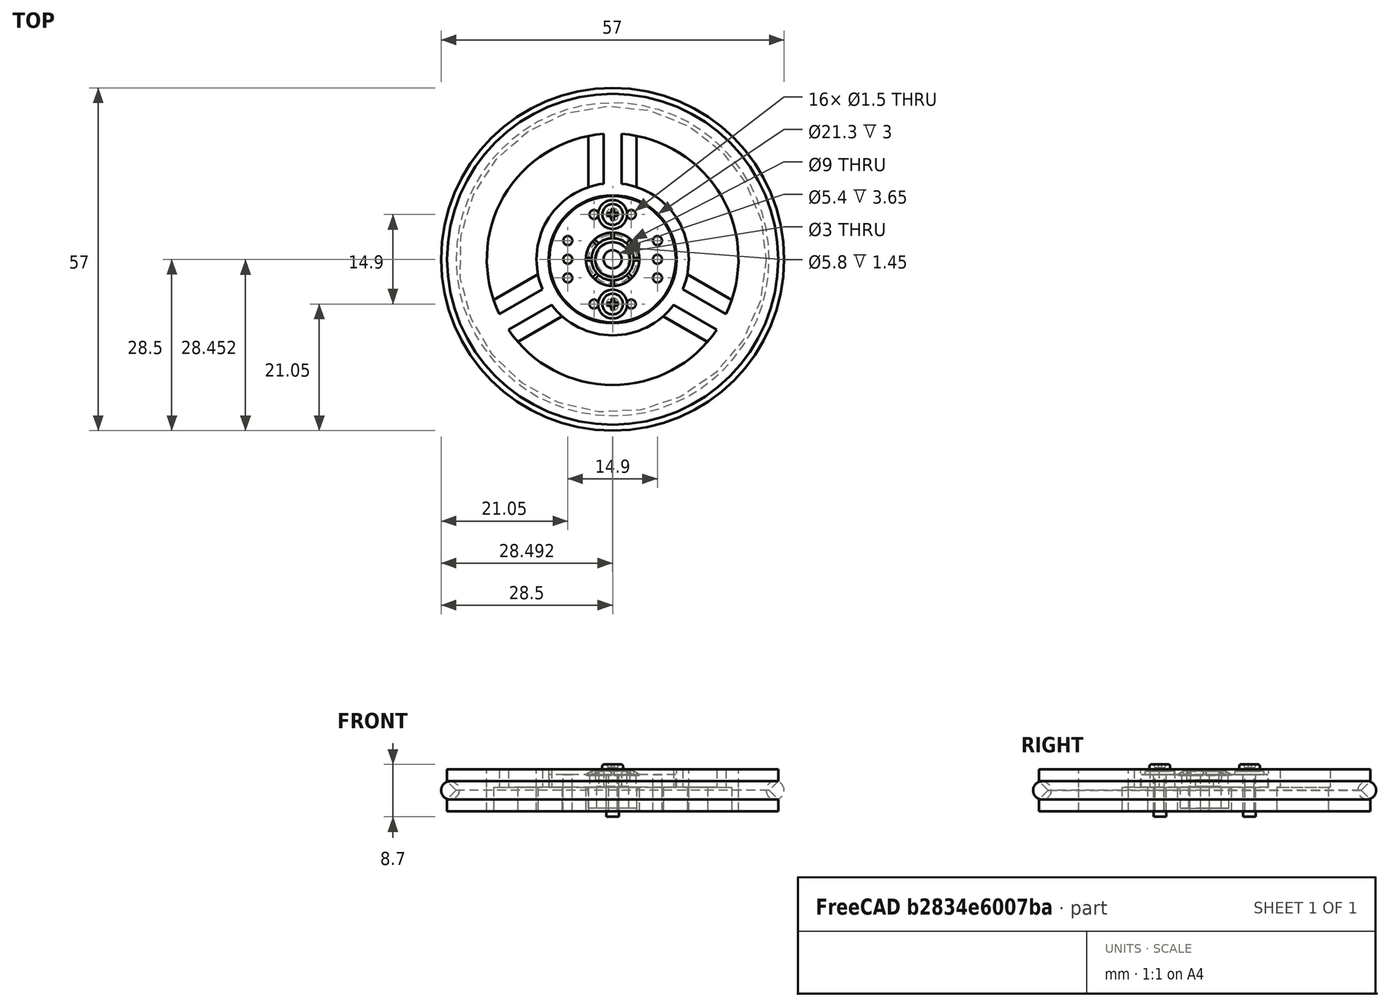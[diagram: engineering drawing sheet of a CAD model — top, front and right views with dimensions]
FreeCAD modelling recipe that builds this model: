
FCSTD DOCUMENT  (FreeCAD 0.14R3702 (Git))
Label: Miniskybot-wheel-renacuajo-futaba3003-assembly
License: CC-BY 3.0
LicenseURL: http://creativecommons.org/licenses/by/3.0/
objects: Part::Feature×4, Part::Torus×1, Part::Compound×1
note: 6 computed .brp shape members not serialized (recipe doc carries the construction recipe); baked Part::Feature solids carry a one-line shape summary decoded from their .brp

FEATURE [Part::Feature] PolarPattern  label="Wheel-renacuajo"
  Placement = pos=(0,0,0) rot=(1,0,0;1.5708rad)
  shape: bbox 55 x 55 x 7 mm, 43 faces (baked)
FEATURE [Part::Feature] Fillet  label="servo-rounded-horn"
  Placement = pos=(0,0,-3) rot=(1,0,0;1.5708rad)
  shape: bbox 21 x 21 x 6.2 mm, 65 faces (baked)
FEATURE [Part::Torus] Torus  label="o-ring"
  Angle1 = -180
  Angle2 = 180
  Angle3 = 360
  Radius1 = 27
  Radius2 = 1.5
FEATURE [Part::Feature] Fillet001  label="bolt-1"
  Placement = pos=(0,7.45,2.6) rot=(0,0,1;0rad)
  shape: bbox 4.8 x 4.8 x 8.7 mm, 21 faces (baked)
FEATURE [Part::Feature] Fillet002  label="bolt-2"
  Placement = pos=(0,-7.45,2.6) rot=(0,0,1;0rad)
  shape: bbox 4.8 x 4.8 x 8.7 mm, 21 faces (baked)
FEATURE [Part::Compound] Compound  label="Miniskybot-wheel-renacuajo-futaba-3003-assembly"
  Links = -> [PolarPattern,Fillet002,Torus,Fillet,Fillet001]
